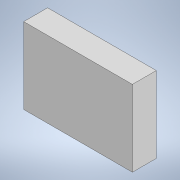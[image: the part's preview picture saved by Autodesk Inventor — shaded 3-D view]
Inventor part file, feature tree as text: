
AUTODESK INVENTOR PART (.ipt)
format: ipt  version: 2020 (Build 240168000, 168)  size: 89,088 bytes
history: native  units: mm
features: extrude x1, sketch x1
ambient origin geometry x8: Origin, YZ Plane, XZ Plane, XY Plane, X Axis, Y Axis, Z Axis, Center Point
bodies: Solide1 (feature_tree)
feature tree (2):
  extrude  "Extrusion1"  Depth=100.0mm
  sketch  "Esquisse1"
